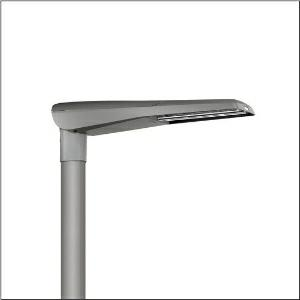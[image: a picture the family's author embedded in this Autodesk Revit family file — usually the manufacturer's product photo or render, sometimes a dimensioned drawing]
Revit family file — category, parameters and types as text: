
# Revit family: streetlight_sl_11_iq_mini___p1_0a_5xc2cc1f08ge_b649
name_source: partatom
category: Lighting Fixtures
units: mm (PartAtom-declared; Revit-internal decimal feet)

## family parameters
Cut with Voids When Loaded = No
Host = Face
Light Source = No
Part Type = Normal
Room Calculation Point = No
Round Connector Dimension = Use Diameter
Shared = No

## types (1)
- --- (1 x LED, 2590 lm, 21.6 W, 2200K)
    Apparent Load = 22 VA
    CIE Flux Codes = 28 62 91 100 100
    Color Rendering = 70
    Color Temperature = 2200K
    Default Elevation = 1800 mm
    Description = Streetlight SL 11 iQ mini, mast luminaire, primary light control with 3 zone facetted reflector, of plastic, silver coated, highly specular, primary optical cover: cover, of PMMA, transparent, light distribution: P1.0a, light emission: direct distribution, primary light characteristic: asymmetric, installation type: post-top, side-entry, lamps: LED, High Power LED, rated values: 3.030lm | 21,3W | 142,3lm/W (begin service life); end service life: 3.030lm | 21,9W; at 50% lumin. flux: 1.515lm | 11,2W | 135,3lm/W, colour temperature: 2200/2700/3000/4000K, colour rendering: CRI > 70, light colour: 722/727/730/740, light setting 1 begin service life: 100% | 3.030lm | 21,3W | 142,3lm/W | 3.000K, light setting 1 end service life: 21,9W, further light settings possible, control: Street-Remote, Auto-Match, Temp-Guard, Lumen-Switch, Night-Set, Smart-Wire, Light-Fading, Desk-Remote (wireless, voltage-free reading and setting of iQ features in the workshop via application-optimized NFC function/RFID function), optimised constant luminous flux control (CLO 2.0), with cable H07RN-F 5x 1.5mm², mains connection: 230..240V, AC, 50/60Hz, connection cable pre-assembled, cable length: 6,5m, luminaire housing, of diecast aluminium, powder-coated, Siteco® metallic grey (DB 702S), please order mast flange separately, inclination adjustable without tools: 0°, 5°, 10°, 15° (post-top) | 0°, -5°, -10°, -15° (side-entry), sealing non-destructively replaceable, multi-level sealing system, length: 736mm, width: 174mm, height: 116mm, mast flange for spigot size: 42mm (side-entry): 5XC10008XM4, 60/48mm (side-entry/post-top): 5XC10108XM2, 76/60mm (side-entry/post-top): 5XC10108XM1, equipment: standard, protection rating (complete): IP66, insulation class (complete): insulation class II (safety insulation), certification: CE, ENEC, ENEC+, VDE, impact resistance: IK10, permissible operating ambient temperature for outdoor applications: -25..+50°C, standard-compliant lighting for roads and squares, Environmental Product Declaration (EPD) tested and certified by an independent institute, packaging unit: 1 piece

Light Distribution: P1.0a
    Height = 116 mm
    Lamp = 1 x LED
    Lamp Light Flux = 2590 lm
    Lamp Power = 21.6 W
    Lamp count = 1
    Length = 736 mm
    Luminous efficacy = 120 lm/W
    Manufacturer = Siteco
    ModVariant = No
    Model = 5XC2CC1F08GE
    Number of Poles = 1
    OnlyDefault = Yes
    Power Factor = 1
    Product Name = Streetlight SL 11 iQ mini | P1.0a
    Product group = mast luminaire | pylon top
    ProductGroupID = 6100
    Protection Class = Protection class II
    Protection Degree = IP 66
    RLX_Detail_Level = 1
    RLX_Emergency_Light_Flux = 0 lm
    RLX_Emergency_Type = 0
    RLX_Emergency_Type_DB = No
    RlxData = <blob elided: 53033 chars, md5=dc43cd54>
    Socket = socket
    Standby Power = 0 W
    System Light Flux = 2590 lm
    System Power = 22 W
    Type Comments = individual setting: luminous flux: 100 % | dim-lin: 254 | 299 mA
    Type Image = l_1003508.jpg
    URL = http://relux.com
    VarID = @adj_037362
    Voltage = 0 V
    Weight = 0.00 kg
    Width = 174 mm

## geometry (parser evidence)
native form markers: Blend x4, Sweep x10
no freeform markers — native parametric forms only
